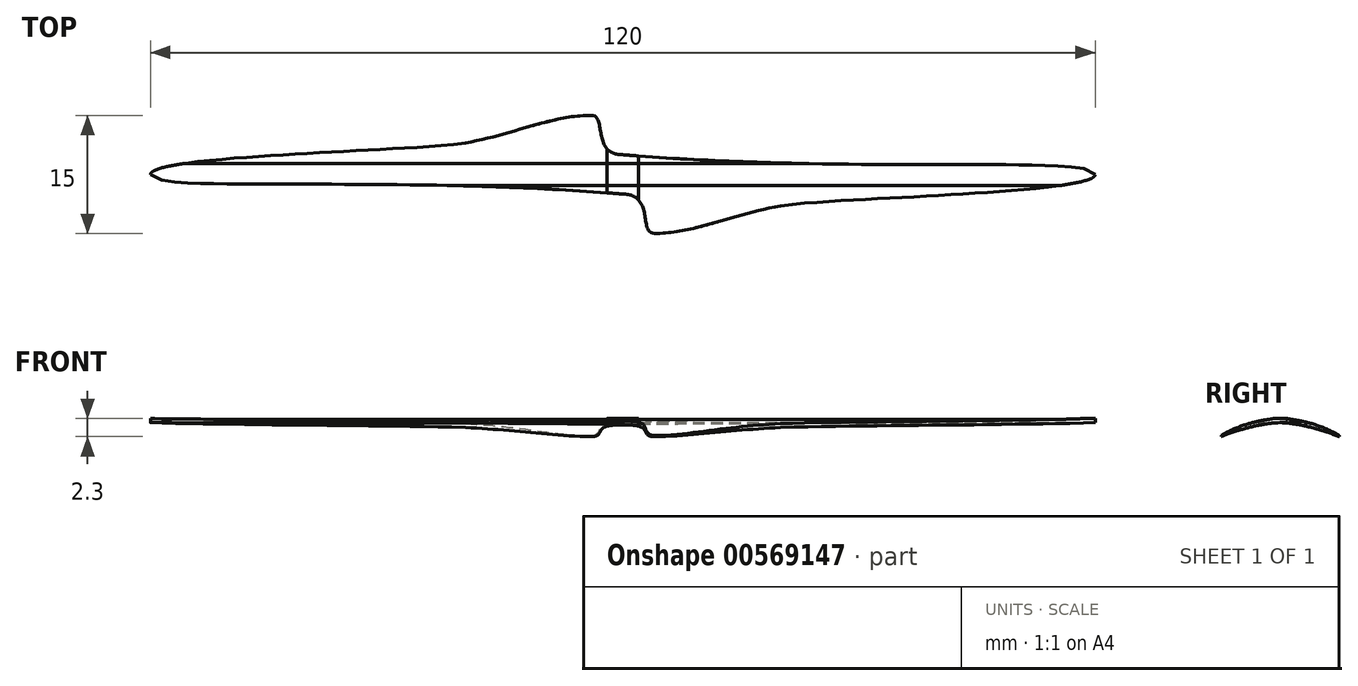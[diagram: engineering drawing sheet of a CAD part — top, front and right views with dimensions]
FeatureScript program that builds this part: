
annotation { "Feature Type Name" : "Feature", "Feature Type Description" : "" }
export const myFeature = defineFeature(function(context is Context, id is Id, definition is map)
    precondition{}
    {
        {
            var Q0;
            Q0=qCreatedBy(makeId("Top.planeOp"),FACE);
            var sketch = newSketch(context, id + "F0", { "sketchPlane" : qUnion([Q0])});
            skLineSegment(sketch, "E0", {"start": v(0, 7.5) * mm, "end": v(0, -7.5) * mm, "construction": true});
            skLineSegment(sketch, "E1", {"start": v(60, 0) * mm, "end": v(-60, 0) * mm, "construction": true});
            skPoint(sketch, "E2", {"position": v(0, 2.5) * mm});
            skPoint(sketch, "E3", {"position": v(0, -2.5) * mm});
            skFitSpline(sketch, "E4", {"points": [v(0, 2.5) * mm, v(-4, 7.5) * mm], "startDerivative": vector(-12, 0) * mm, "endDerivative": vector(-6, 0) * mm});
            skFitSpline(sketch, "E5", {"points": [v(-4, 7.5) * mm, v(-20, 4) * mm], "startDerivative": vector(-15, 0) * mm, "endDerivative": vector(-17.73, -3.13) * mm});
            skFitSpline(sketch, "E6", {"points": [v(-60, 0) * mm, v(0, -2.5) * mm], "startDerivative": vector(0, -7.5) * mm, "endDerivative": vector(90, -7.5) * mm});
            skFitSpline(sketch, "E7", {"points": [v(-20, 4) * mm, v(-60, 0) * mm], "startDerivative": vector(-17.73, -3.13) * mm, "endDerivative": vector(0, -7.5) * mm});
            skLineSegment(sketch, "E8", {"start": v(-25.9, 2.96) * mm, "end": v(-14.1, 5.04) * mm, "construction": true});
            skPoint(sketch, "E9", {"position": v(0, 4) * mm});
            skPoint(sketch, "E10", {"position": v(0, -4) * mm});
            skFitSpline(sketch, "E11.MirrorCS", {"points": [v(0, 2.5) * mm, v(4, 7.5) * mm], "startDerivative": vector(12, 0) * mm, "endDerivative": vector(6, 0) * mm, "construction": true});
            skFitSpline(sketch, "E12.MirrorCS", {"points": [v(4, 7.5) * mm, v(20, 4) * mm], "startDerivative": vector(15, 0) * mm, "endDerivative": vector(17.73, -3.13) * mm, "construction": true});
            skFitSpline(sketch, "E13.MirrorCS", {"points": [v(20, 4) * mm, v(60, 0) * mm], "startDerivative": vector(17.73, -3.13) * mm, "endDerivative": vector(0, -7.5) * mm, "construction": true});
            skFitSpline(sketch, "E14.MirrorCS", {"points": [v(60, 0) * mm, v(0, -2.5) * mm], "startDerivative": vector(0, -7.5) * mm, "endDerivative": vector(-90, -7.5) * mm, "construction": true});
            skFitSpline(sketch, "E15.MirrorCS", {"points": [v(0, -2.5) * mm, v(4, -7.5) * mm], "startDerivative": vector(12, 0) * mm, "endDerivative": vector(6, 0) * mm});
            skFitSpline(sketch, "E16.MirrorCS", {"points": [v(4, -7.5) * mm, v(20, -4) * mm], "startDerivative": vector(15, 0) * mm, "endDerivative": vector(17.73, 3.13) * mm});
            skFitSpline(sketch, "E17.MirrorCS", {"points": [v(20, -4) * mm, v(60, 0) * mm], "startDerivative": vector(17.73, 3.13) * mm, "endDerivative": vector(0, 7.5) * mm});
            skFitSpline(sketch, "E18.MirrorCS", {"points": [v(60, 0) * mm, v(0, 2.5) * mm], "startDerivative": vector(0, 7.5) * mm, "endDerivative": vector(-90, 7.5) * mm});
            skSolve(sketch);
        }
        {
            var Q0;
            Q0=qCreatedBy(makeId("Right.planeOp"),FACE);
            var sketch = newSketch(context, id + "F1", { "sketchPlane" : qUnion([Q0])});
            skLineSegment(sketch, "E19.0", {"start": v(0, 5) * mm, "end": v(0, -5) * mm, "construction": true});
            skLineSegment(sketch, "E20.0", {"start": v(40, 0) * mm, "end": v(-40, 0) * mm, "construction": true});
            skFitSpline(sketch, "E21", {"points": [v(0.5, 0) * mm, v(2.5, -0.8) * mm], "startDerivative": vector(3, 0) * mm, "endDerivative": vector(0, -0.9) * mm});
            skFitSpline(sketch, "E22", {"points": [v(2.5, -0.8) * mm, v(-8, -2.5) * mm], "startDerivative": vector(-4.44, 1.37) * mm, "endDerivative": vector(-17.2, -6.92) * mm});
            skFitSpline(sketch, "E23", {"points": [v(0.5, 0) * mm, v(-8, -2.5) * mm], "startDerivative": vector(-9, 0) * mm, "endDerivative": vector(-6.5, -4.53) * mm});
            skFitSpline(sketch, "E24.MirrorCS", {"points": [v(-2.5, -0.8) * mm, v(8, -2.5) * mm], "startDerivative": vector(4.44, 1.37) * mm, "endDerivative": vector(17.2, -6.92) * mm});
            skFitSpline(sketch, "E25.MirrorCS", {"points": [v(-0.5, 0) * mm, v(8, -2.5) * mm], "startDerivative": vector(9, 0) * mm, "endDerivative": vector(6.5, -4.53) * mm});
            skFitSpline(sketch, "E26.MirrorCS", {"points": [v(-0.5, 0) * mm, v(-2.5, -0.8) * mm], "startDerivative": vector(-3, 0) * mm, "endDerivative": vector(0, -0.9) * mm});
            skSolve(sketch);
        }
        {
            var Q0;
            {var subQ0=sQuery(id+"F1.wireOp",EDGE,"E23");var subQ1=sQuery(id+"F1.wireOp",EDGE,"E22");var subQ2=makeQuery(id+"F1.imprint","INTERSECT",VERTEX,{"derivedFrom":[subQ1,subQ0]});Q0=makeQuery(id+"F1.imprint","IMPRINT",FACE,{"disambiguationData":[TD([[makeQuery(id+"F1.imprint","IMPRINT",EDGE,{"disambiguationData":[TD([[subQ2,1.0]])],"derivedFrom":subQ1}),-1.0]])]});}
            var Q1;
            {var subQ7=sQuery(id+"F1.wireOp",EDGE,"E22");var subQ9=sQuery(id+"F1.wireOp",EDGE,"E21");var subQ10=makeQuery(id+"F1.imprint","INTERSECT",VERTEX,{"derivedFrom":[subQ9,subQ7]});Q1=makeQuery(id+"F1.imprint","IMPRINT",FACE,{"disambiguationData":[TD([[makeQuery(id+"F1.imprint","IMPRINT",EDGE,{"disambiguationData":[TD([[subQ10,1.0]])],"derivedFrom":subQ9}),-1.0]])]});}
            var Q2;
            {var subQ0=sQuery(id+"F1.wireOp",EDGE,"E25.MirrorCS");var subQ1=sQuery(id+"F1.wireOp",EDGE,"E23");var subQ2=makeQuery(id+"F1.imprint","INTERSECT",VERTEX,{"derivedFrom":[subQ1,subQ0]});Q2=makeQuery(id+"F1.imprint","IMPRINT",FACE,{"disambiguationData":[TD([[makeQuery(id+"F1.imprint","IMPRINT",EDGE,{"disambiguationData":[TD([[subQ2,-1.0]])],"derivedFrom":subQ1}),-1.0]])]});}
            extrude(context, id + "F2", {"entities" : qUnion([Q0, Q1, Q2]), "depth" : 120 * mm, "offsetDistance" : 25 * mm, "hasSecondDirection" : true, "secondDirectionOppositeDirection" : false, "secondDirectionDepth" : 2 * mm});
        }
        {
            var Q0;
            {var subQ0=sQuery(id+"F1.wireOp",EDGE,"E22");var subQ1=sQuery(id+"F1.wireOp",EDGE,"E21");var subQ2=makeQuery(id+"F1.imprint","INTERSECT",VERTEX,{"derivedFrom":[subQ1,subQ0]});Q0=makeQuery(id+"F1.imprint","IMPRINT",FACE,{"disambiguationData":[TD([[makeQuery(id+"F1.imprint","IMPRINT",EDGE,{"disambiguationData":[TD([[subQ2,1.0]])],"derivedFrom":subQ1}),1.0]])]});}
            var Q1;
            {var subQ7=sQuery(id+"F1.wireOp",EDGE,"E22");var subQ9=sQuery(id+"F1.wireOp",EDGE,"E21");var subQ10=makeQuery(id+"F1.imprint","INTERSECT",VERTEX,{"derivedFrom":[subQ9,subQ7]});Q1=makeQuery(id+"F1.imprint","IMPRINT",FACE,{"disambiguationData":[TD([[makeQuery(id+"F1.imprint","IMPRINT",EDGE,{"disambiguationData":[TD([[subQ10,1.0]])],"derivedFrom":subQ9}),-1.0]])]});}
            var Q2;
            {var subQ0=sQuery(id+"F1.wireOp",EDGE,"E23");var subQ1=sQuery(id+"F1.wireOp",EDGE,"E21");var subQ2=makeQuery(id+"F1.imprint","INTERSECT",VERTEX,{"derivedFrom":[subQ1,subQ0]});Q2=makeQuery(id+"F1.imprint","IMPRINT",FACE,{"disambiguationData":[TD([[makeQuery(id+"F1.imprint","IMPRINT",EDGE,{"disambiguationData":[TD([[subQ2,-1.0]])],"derivedFrom":subQ1}),-1.0]])]});}
            extrude(context, id + "F3", {"entities" : qUnion([Q0, Q1, Q2]), "oppositeDirection" : true, "depth" : 120 * mm, "offsetDistance" : 25 * mm, "hasSecondDirection" : true, "secondDirectionOppositeDirection" : true, "secondDirectionDepth" : 2 * mm});
        }
        {
            var Q0;
            Q0=makeQuery(id+"F2.opExtrude","CAP_FACE",FACE,{"disambiguationData":[OSD([sQuery(id+"F1.wireOp",EDGE,"E21"),sQuery(id+"F1.wireOp",EDGE,"E22"),sQuery(id+"F1.wireOp",EDGE,"E23"),sQuery(id+"F1.wireOp",EDGE,"E25.MirrorCS"),sQuery(id+"F1.wireOp",EDGE,"E26.MirrorCS")])],"isStart":true});
            var Q1;
            Q1=makeQuery(id+"F3.opExtrude","CAP_FACE",FACE,{"disambiguationData":[OSD([sQuery(id+"F1.wireOp",EDGE,"E21"),sQuery(id+"F1.wireOp",EDGE,"E23"),sQuery(id+"F1.wireOp",EDGE,"E24.MirrorCS"),sQuery(id+"F1.wireOp",EDGE,"E25.MirrorCS"),sQuery(id+"F1.wireOp",EDGE,"E26.MirrorCS")])],"isStart":true});
            loft(context, id + "F4", {"sheetProfilesArray" : [{ "sheetProfileEntities" : qUnion([Q0]) }, { "sheetProfileEntities" : qUnion([Q1]) }]});
        }
        {
            var Q0;
            Q0=makeQuery(id+"F0.imprint","IMPRINT",FACE,{"disambiguationData":[TD([[makeQuery(id+"F0.imprint","IMPRINT",EDGE,{"derivedFrom":sQuery(id+"F0.wireOp",EDGE,"E4")}),1.0]])]});
            extrude(context, id + "F5", {"entities" : qUnion([Q0]), "operationType" : NewBodyOperationType.INTERSECT, "oppositeDirection" : true, "depth" : 4 * mm, "offsetDistance" : 25 * mm});
        }
    });
